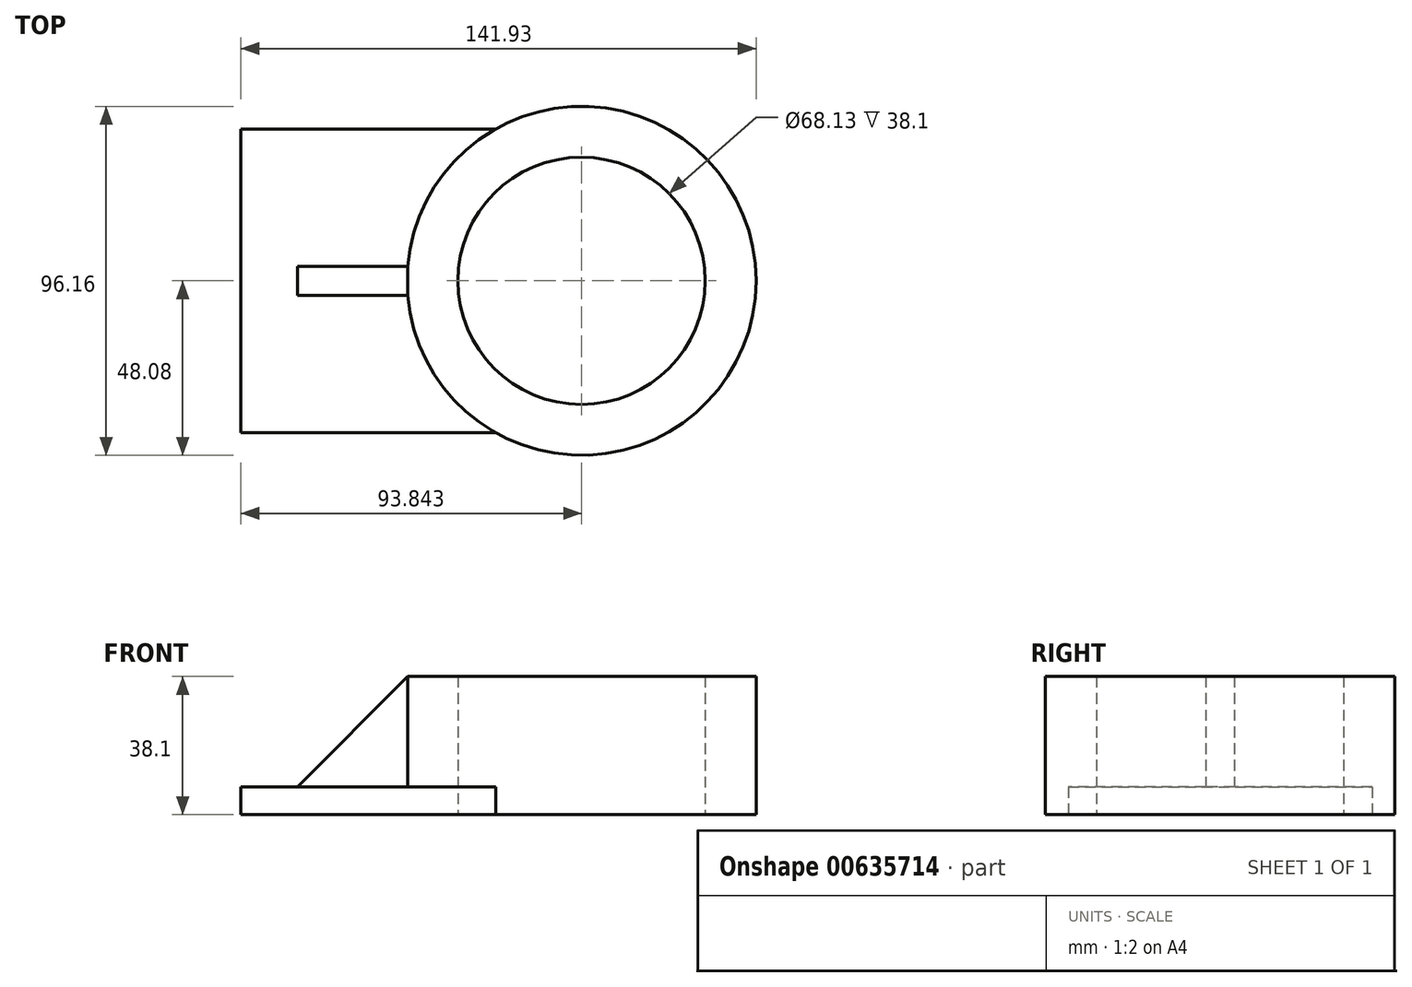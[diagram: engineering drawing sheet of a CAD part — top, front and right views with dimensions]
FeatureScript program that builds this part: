
annotation { "Feature Type Name" : "Feature", "Feature Type Description" : "" }
export const myFeature = defineFeature(function(context is Context, id is Id, definition is map)
    precondition{}
    {
        {
            var Q0;
            Q0=qCreatedBy(makeId("Top.planeOp"),FACE);
            var sketch = newSketch(context, id + "F0", { "sketchPlane" : qUnion([Q0])});
            skLineSegment(sketch, "E0.bottom", {"start": v(45.76, -41.84) * mm, "end": v(-45.76, -41.84) * mm});
            skLineSegment(sketch, "E0.top", {"start": v(45.76, 41.84) * mm, "end": v(-45.76, 41.84) * mm});
            skLineSegment(sketch, "E0.right", {"start": v(-45.76, -41.84) * mm, "end": v(-45.76, 41.84) * mm});
            skPoint(sketch, "E0.middle", {"position": v(0, 0) * mm});
            skArc(sketch, "E1", {"start": v(45.76, 41.84) * mm, "mid": v(3.91, 0) * mm, "end": v(45.76, -41.84) * mm});
            skSolve(sketch);
        }
        {
            var Q0;
            Q0=makeQuery(id+"F0.imprint","IMPRINT",FACE,{"disambiguationData":[TD([[makeQuery(id+"F0.imprint","IMPRINT",EDGE,{"derivedFrom":sQuery(id+"F0.wireOp",EDGE,"E0.bottom")}),-1.0]])]});
            extrude(context, id + "F1", {"entities" : qUnion([Q0]), "depth" : 7.62 * mm, "offsetDistance" : 25.4 * mm});
        }
        {
            var Q0;
            Q0=qCreatedBy(makeId("Top.planeOp"),FACE);
            var sketch = newSketch(context, id + "F2", { "sketchPlane" : qUnion([Q0])});
            skCircle(sketch, "E2", {"center": v(48.08, 0) * mm, "radius": 48.08 * mm});
            skCircle(sketch, "E3", {"center": v(48.08, 0) * mm, "radius": 34.07 * mm});
            skSolve(sketch);
        }
        {
            var Q0;
            Q0 = qSketchRegion(id + "F2", true);
            extrude(context, id + "F3", {"entities" : qUnion([Q0]), "operationType" : NewBodyOperationType.ADD, "depth" : 38.1 * mm, "offsetDistance" : 25.4 * mm});
        }
        {
            var Q0;
            Q0=makeQuery(id+"F1.opExtrude","CAP_FACE",FACE,{"disambiguationData":[OSD([sQuery(id+"F0.wireOp",EDGE,"E0.bottom"),sQuery(id+"F0.wireOp",EDGE,"E0.top"),sQuery(id+"F0.wireOp",EDGE,"E0.right"),sQuery(id+"F0.wireOp",EDGE,"E1")])],"isStart":false});
            var sketch = newSketch(context, id + "F4", { "sketchPlane" : qUnion([Q0])});
            skLineSegment(sketch, "E4.bottom", {"start": v(0.16, 3.98) * mm, "end": v(-30.13, 3.98) * mm});
            skLineSegment(sketch, "E4.top", {"start": v(0.16, -3.98) * mm, "end": v(-30.13, -3.98) * mm});
            skLineSegment(sketch, "E4.left", {"start": v(0.16, 3.98) * mm, "end": v(0.16, -3.98) * mm});
            skPoint(sketch, "E4.middle", {"position": v(-45.76, 0) * mm});
            skPoint(sketch, "E4.right.end.orphan", {"position": v(-91.68, -3.98) * mm});
            skPoint(sketch, "E4.right.start.orphan", {"position": v(-91.68, 3.98) * mm});
            skLineSegment(sketch, "E5", {"start": v(-30.13, 3.98) * mm, "end": v(-30.13, -3.98) * mm});
            skPoint(sketch, "E6.orphan", {"position": v(-45.76, 3.98) * mm});
            skPoint(sketch, "E7.end.orphan", {"position": v(-45.76, -3.98) * mm});
            skSolve(sketch);
        }
        {
            var Q0;
            {var subQ0=sQuery(id+"F4.wireOp",EDGE,"E4.left");Q0=makeQuery(id+"F4.imprint","IMPRINT",FACE,{"disambiguationData":[TD([[makeQuery(id+"F4.imprint","IMPRINT",EDGE,{"derivedFrom":subQ0}),-1.0]])]});}
            var Q1;
            {var subQ0=sQuery(id+"F4.wireOp",EDGE,"E4.bottom");Q1=makeQuery(id+"F4.imprint","IMPRINT",FACE,{"disambiguationData":[TD([[makeQuery(id+"F4.imprint","IMPRINT",EDGE,{"derivedFrom":subQ0}),1.0]])]});}
            extrude(context, id + "F5", {"entities" : qUnion([Q0, Q1]), "operationType" : NewBodyOperationType.ADD, "depth" : 38.1 * mm, "offsetDistance" : 25.4 * mm});
        }
        {
            var Q0;
            Q0=makeQuery(id+"F5.opExtrude","SWEPT_FACE",FACE,{"disambiguationData":[OSD([sQuery(id+"F4.wireOp",EDGE,"E4.top")])]});
            var sketch = newSketch(context, id + "F6", { "sketchPlane" : qUnion([Q0])});
            skLineSegment(sketch, "E8", {"start": v(0.16, 38.1) * mm, "end": v(-30.13, 7.62) * mm});
            skSolve(sketch);
        }
        {
            var Q0;
            Q0=makeQuery(id+"F6.imprint","IMPRINT",FACE,{"disambiguationData":[TD([[makeQuery(id+"F6.imprint","IMPRINT",EDGE,{"derivedFrom":sQuery(id+"F6.wireOp",EDGE,"E8")}),-1.0]])]});
            extrude(context, id + "F7", {"entities" : qUnion([Q0]), "operationType" : NewBodyOperationType.REMOVE, "endBound" : BoundingType.THROUGH_ALL, "oppositeDirection" : true, "depth" : 25.4 * mm, "offsetDistance" : 25.4 * mm});
        }
    });
